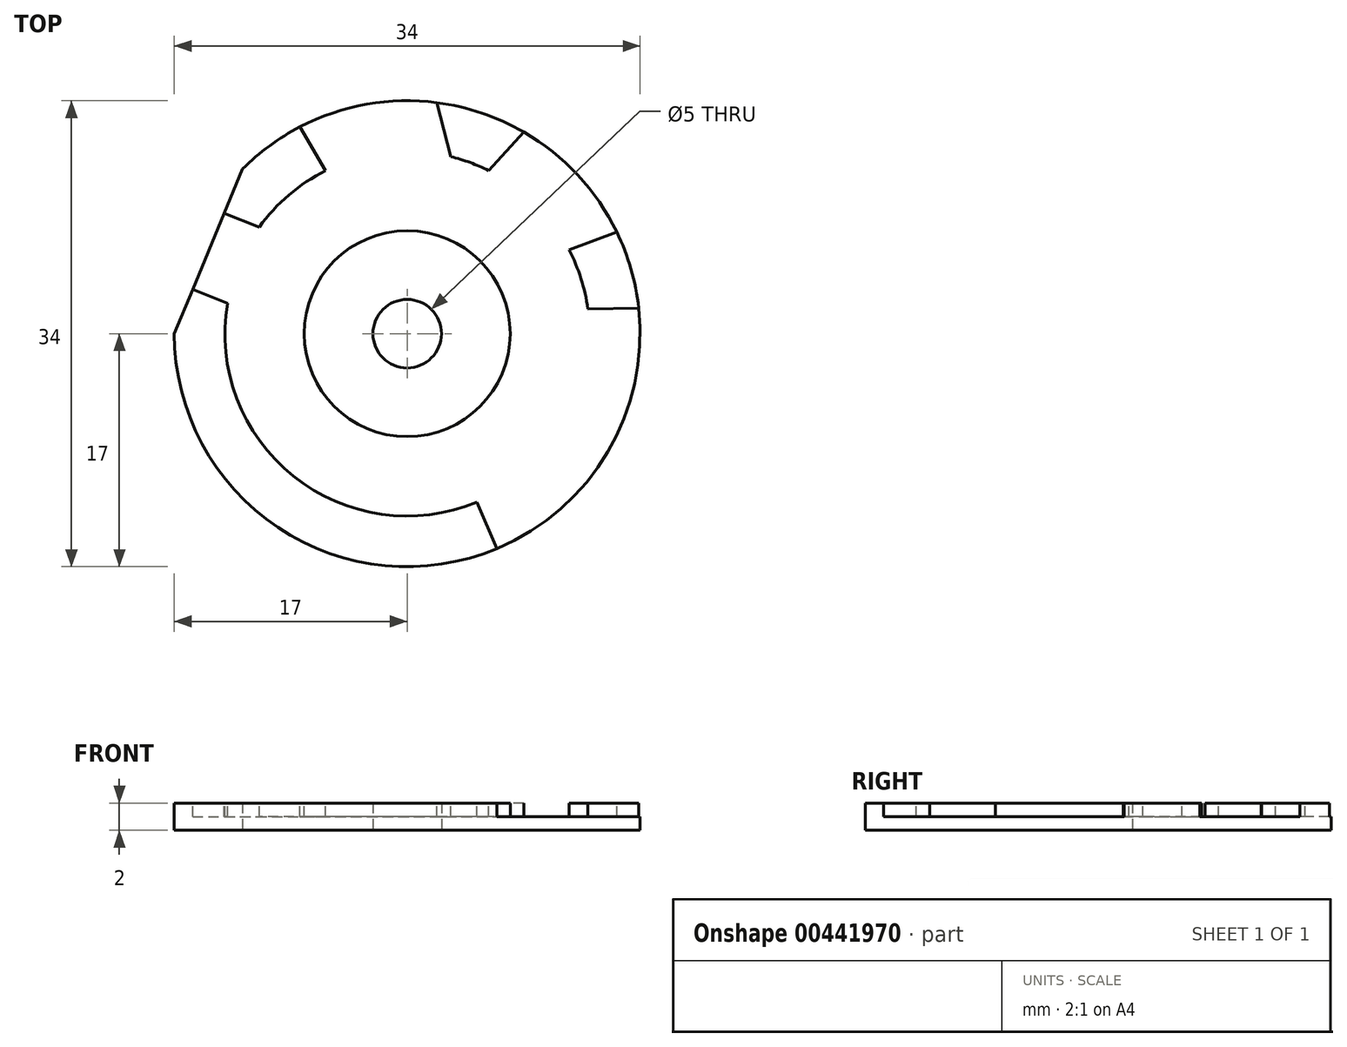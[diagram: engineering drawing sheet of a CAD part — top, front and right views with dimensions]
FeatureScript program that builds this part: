
annotation { "Feature Type Name" : "Feature", "Feature Type Description" : "" }
export const myFeature = defineFeature(function(context is Context, id is Id, definition is map)
    precondition{}
    {
        {
            var Q0;
            Q0=qCreatedBy(makeId("Top.planeOp"),FACE);
            var sketch = newSketch(context, id + "F0", { "sketchPlane" : qUnion([Q0])});
            skCircle(sketch, "E0.cCircle", {"center": v(0, 0) * mm, "radius": 17 * mm, "construction": true});
            skLineSegment(sketch, "E0.0", {"start": v(-17, 0) * mm, "end": v(-12.02, 12.02) * mm});
            skLineSegment(sketch, "E0.1", {"start": v(-12.02, 12.02) * mm, "end": v(0, 17) * mm});
            skLineSegment(sketch, "E0.2", {"start": v(0, 17) * mm, "end": v(12.02, 12.02) * mm});
            skLineSegment(sketch, "E0.3", {"start": v(12.02, 12.02) * mm, "end": v(17, 0) * mm});
            skLineSegment(sketch, "E0.4", {"start": v(17, 0) * mm, "end": v(12.02, -12.02) * mm});
            skLineSegment(sketch, "E0.5", {"start": v(12.02, -12.02) * mm, "end": v(0, -17) * mm});
            skLineSegment(sketch, "E0.6", {"start": v(0, -17) * mm, "end": v(-12.02, -12.02) * mm});
            skLineSegment(sketch, "E0.7", {"start": v(-12.02, -12.02) * mm, "end": v(-17, 0) * mm});
            skCircle(sketch, "E1", {"center": v(0, 0) * mm, "radius": 2.5 * mm});
            skPoint(sketch, "E2", {"position": v(0, 2.5) * mm});
            skCircle(sketch, "E3", {"center": v(0, 0) * mm, "radius": 17 * mm});
            skSolve(sketch);
        }
        {
            var Q0;
            Q0=makeQuery(id+"F0.imprint","IMPRINT",FACE,{"disambiguationData":[TD([[makeQuery(id+"F0.imprint","IMPRINT",EDGE,{"derivedFrom":sQuery(id+"F0.wireOp",EDGE,"E0.0")}),-1.0]])]});
            var Q1;
            {var subQ0=sQuery(id+"F0.wireOp",EDGE,"E0.7");Q1=makeQuery(id+"F0.imprint","IMPRINT",FACE,{"disambiguationData":[TD([[makeQuery(id+"F0.imprint","IMPRINT",EDGE,{"derivedFrom":subQ0}),1.0]])]});}
            var Q2;
            {var subQ0=sQuery(id+"F0.wireOp",EDGE,"E0.6");Q2=makeQuery(id+"F0.imprint","IMPRINT",FACE,{"disambiguationData":[TD([[makeQuery(id+"F0.imprint","IMPRINT",EDGE,{"derivedFrom":subQ0}),1.0]])]});}
            var Q3;
            {var subQ0=sQuery(id+"F0.wireOp",EDGE,"E0.2");Q3=makeQuery(id+"F0.imprint","IMPRINT",FACE,{"disambiguationData":[TD([[makeQuery(id+"F0.imprint","IMPRINT",EDGE,{"derivedFrom":subQ0}),1.0]])]});}
            var Q4;
            {var subQ0=sQuery(id+"F0.wireOp",EDGE,"E0.1");Q4=makeQuery(id+"F0.imprint","IMPRINT",FACE,{"disambiguationData":[TD([[makeQuery(id+"F0.imprint","IMPRINT",EDGE,{"derivedFrom":subQ0}),1.0]])]});}
            var Q5;
            {var subQ0=sQuery(id+"F0.wireOp",EDGE,"E0.5");Q5=makeQuery(id+"F0.imprint","IMPRINT",FACE,{"disambiguationData":[TD([[makeQuery(id+"F0.imprint","IMPRINT",EDGE,{"derivedFrom":subQ0}),1.0]])]});}
            var Q6;
            {var subQ0=sQuery(id+"F0.wireOp",EDGE,"E0.4");Q6=makeQuery(id+"F0.imprint","IMPRINT",FACE,{"disambiguationData":[TD([[makeQuery(id+"F0.imprint","IMPRINT",EDGE,{"derivedFrom":subQ0}),1.0]])]});}
            var Q7;
            {var subQ0=sQuery(id+"F0.wireOp",EDGE,"E0.3");Q7=makeQuery(id+"F0.imprint","IMPRINT",FACE,{"disambiguationData":[TD([[makeQuery(id+"F0.imprint","IMPRINT",EDGE,{"derivedFrom":subQ0}),1.0]])]});}
            extrude(context, id + "F1", {"entities" : qUnion([Q0, Q1, Q2, Q3, Q4, Q5, Q6, Q7]), "depth" : 2 * mm, "offsetDistance" : 25.4 * mm});
        }
        {
            var Q0;
            Q0=makeQuery(id+"F1.opExtrude","CAP_FACE",FACE,{"disambiguationData":[OSD([sQuery(id+"F0.wireOp",EDGE,"E0.0"),sQuery(id+"F0.wireOp",EDGE,"E1"),sQuery(id+"F0.wireOp",EDGE,"E3")])],"isStart":false});
            var sketch = newSketch(context, id + "F2", { "sketchPlane" : qUnion([Q0])});
            skCircle(sketch, "E4", {"center": v(0, 0) * mm, "radius": 7.52 * mm});
            skCircle(sketch, "E5", {"center": v(0, 0) * mm, "radius": 13.3 * mm});
            skPoint(sketch, "E6", {"position": v(-14.51, 6.01) * mm});
            skPoint(sketch, "E7", {"position": v(-13.36, 8.78) * mm});
            skPoint(sketch, "E8", {"position": v(-15.66, 3.24) * mm});
            skPoint(sketch, "E9", {"position": v(-13.12, 2.23) * mm});
            skLineSegment(sketch, "E10", {"start": v(-15.66, 3.24) * mm, "end": v(-13.12, 2.23) * mm});
            skPoint(sketch, "E11", {"position": v(-10.8, 7.78) * mm});
            skLineSegment(sketch, "E12", {"start": v(-13.36, 8.78) * mm, "end": v(-10.8, 7.78) * mm});
            skPoint(sketch, "E13", {"position": v(-5.97, 11.9) * mm});
            skPoint(sketch, "E14", {"position": v(-7.83, 15.1) * mm});
            skPoint(sketch, "E15", {"position": v(11.82, 6.12) * mm});
            skPoint(sketch, "E16", {"position": v(15.3, 7.42) * mm});
            skLineSegment(sketch, "E17", {"start": v(-7.83, 15.1) * mm, "end": v(-5.97, 11.9) * mm});
            skLineSegment(sketch, "E18", {"start": v(11.82, 6.12) * mm, "end": v(15.3, 7.42) * mm});
            skPoint(sketch, "E19", {"position": v(16.9, 1.88) * mm});
            skPoint(sketch, "E20", {"position": v(13.19, 1.8) * mm});
            skPoint(sketch, "E21", {"position": v(5.08, -12.3) * mm});
            skPoint(sketch, "E22", {"position": v(6.56, -15.68) * mm});
            skPoint(sketch, "E23", {"position": v(3.18, 12.92) * mm});
            skPoint(sketch, "E24", {"position": v(5.95, 11.9) * mm});
            skPoint(sketch, "E25", {"position": v(8.51, 14.72) * mm});
            skPoint(sketch, "E26", {"position": v(2.18, 16.86) * mm});
            skLineSegment(sketch, "E27", {"start": v(2.18, 16.86) * mm, "end": v(3.18, 12.92) * mm});
            skLineSegment(sketch, "E28", {"start": v(8.51, 14.72) * mm, "end": v(5.95, 11.9) * mm});
            skLineSegment(sketch, "E29", {"start": v(16.9, 1.88) * mm, "end": v(13.19, 1.8) * mm});
            skLineSegment(sketch, "E30", {"start": v(5.08, -12.3) * mm, "end": v(6.56, -15.68) * mm});
            skSolve(sketch);
        }
        {
            var Q0;
            Q0 = qSketchRegion(id + "F2", true);
            var Q1;
            {var subQ0=sQuery(id+"F2.wireOp",EDGE,"E17");Q1=makeQuery(id+"F2.imprint","IMPRINT",FACE,{"disambiguationData":[TD([[makeQuery(id+"F2.imprint","IMPRINT",EDGE,{"derivedFrom":subQ0}),1.0]])]});}
            var Q2;
            {var subQ0=sQuery(id+"F2.wireOp",EDGE,"E10");Q2=makeQuery(id+"F2.imprint","IMPRINT",FACE,{"disambiguationData":[TD([[makeQuery(id+"F2.imprint","IMPRINT",EDGE,{"derivedFrom":subQ0}),1.0]])]});}
            var Q3;
            {var subQ0=sQuery(id+"F2.wireOp",EDGE,"E18");Q3=makeQuery(id+"F2.imprint","IMPRINT",FACE,{"disambiguationData":[TD([[makeQuery(id+"F2.imprint","IMPRINT",EDGE,{"derivedFrom":subQ0}),1.0]])]});}
            var Q4;
            {var subQ0=sQuery(id+"F2.wireOp",EDGE,"E29");Q4=makeQuery(id+"F2.imprint","IMPRINT",FACE,{"disambiguationData":[TD([[makeQuery(id+"F2.imprint","IMPRINT",EDGE,{"derivedFrom":subQ0}),1.0]])]});}
            extrude(context, id + "F3", {"entities" : qUnion([Q0, Q1, Q2, Q3, Q4]), "operationType" : NewBodyOperationType.REMOVE, "oppositeDirection" : true, "depth" : 1 * mm, "offsetDistance" : 25.4 * mm});
        }
    });
